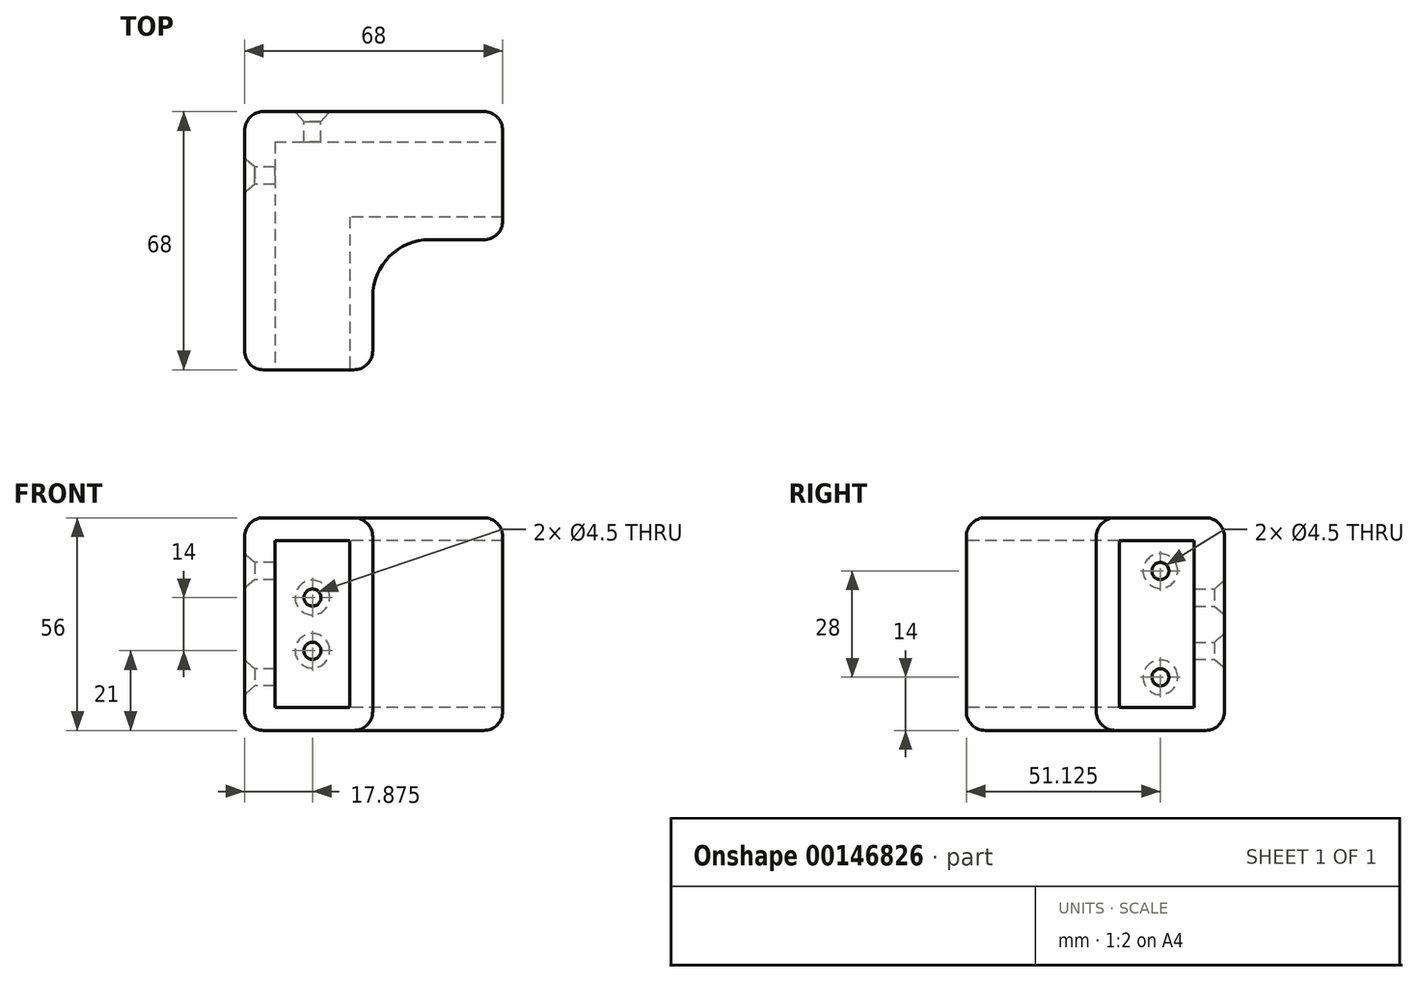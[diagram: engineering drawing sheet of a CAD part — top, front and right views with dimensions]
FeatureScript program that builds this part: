
annotation { "Feature Type Name" : "Feature", "Feature Type Description" : "" }
export const myFeature = defineFeature(function(context is Context, id is Id, definition is map)
    precondition{}
    {
        {
            var Q0;
            Q0=qCreatedBy(makeId("Top.planeOp"),FACE);
            var sketch = newSketch(context, id + "F0", { "sketchPlane" : qUnion([Q0])});
            skLineSegment(sketch, "E0.top", {"start": v(0, -60) * mm, "end": v(19.75, -60) * mm});
            skLineSegment(sketch, "E0.left", {"start": v(0, 0) * mm, "end": v(0, -60) * mm});
            skLineSegment(sketch, "E0.right", {"start": v(19.75, -19.75) * mm, "end": v(19.75, -60) * mm});
            skLineSegment(sketch, "E1", {"start": v(0, 0) * mm, "end": v(60, 0) * mm});
            skLineSegment(sketch, "E2", {"start": v(60, 0) * mm, "end": v(60, -19.75) * mm});
            skLineSegment(sketch, "E3", {"start": v(60, -19.75) * mm, "end": v(19.75, -19.75) * mm});
            skLineSegment(sketch, "E4.0", {"start": v(-8, 8) * mm, "end": v(60, 8) * mm});
            skLineSegment(sketch, "E4.1", {"start": v(-8, 8) * mm, "end": v(-8, -60) * mm});
            skLineSegment(sketch, "E5.0", {"start": v(25.75, -25.75) * mm, "end": v(25.75, -60) * mm});
            skLineSegment(sketch, "E5.1", {"start": v(60, -25.75) * mm, "end": v(25.75, -25.75) * mm});
            skLineSegment(sketch, "E6", {"start": v(-8, -60) * mm, "end": v(0, -60) * mm});
            skLineSegment(sketch, "E7", {"start": v(19.75, -60) * mm, "end": v(25.75, -60) * mm});
            skLineSegment(sketch, "E8", {"start": v(60, -25.75) * mm, "end": v(60, -19.75) * mm});
            skLineSegment(sketch, "E9", {"start": v(60, 0) * mm, "end": v(60, 8) * mm});
            skSolve(sketch);
        }
        {
            var Q0;
            Q0=makeQuery(id+"F0.imprint","IMPRINT",FACE,{"disambiguationData":[TD([[makeQuery(id+"F0.imprint","IMPRINT",EDGE,{"derivedFrom":sQuery(id+"F0.wireOp",EDGE,"E0.left")}),-1.0]])]});
            var Q1;
            Q1=makeQuery(id+"F0.imprint","IMPRINT",FACE,{"disambiguationData":[TD([[makeQuery(id+"F0.imprint","IMPRINT",EDGE,{"derivedFrom":sQuery(id+"F0.wireOp",EDGE,"E0.right")}),1.0]])]});
            var Q2;
            Q2=makeQuery(id+"F0.imprint","IMPRINT",FACE,{"disambiguationData":[TD([[makeQuery(id+"F0.imprint","IMPRINT",EDGE,{"derivedFrom":sQuery(id+"F0.wireOp",EDGE,"E0.top")}),1.0]])]});
            extrude(context, id + "F1", {"entities" : qUnion([Q0, Q1, Q2]), "depth" : 50 * mm, "hasSecondDirection" : true, "secondDirectionOppositeDirection" : true, "secondDirectionDepth" : 6 * mm});
        }
        {
            var Q0;
            Q0=makeQuery(id+"F0.imprint","IMPRINT",FACE,{"disambiguationData":[TD([[makeQuery(id+"F0.imprint","IMPRINT",EDGE,{"derivedFrom":sQuery(id+"F0.wireOp",EDGE,"E0.top")}),1.0]])]});
            extrude(context, id + "F2", {"entities" : qUnion([Q0]), "operationType" : NewBodyOperationType.REMOVE, "depth" : 44 * mm});
        }
        {
            var Q0;
            Q0=makeQuery(id+"F1.opExtrude","SWEPT_FACE",FACE,{"disambiguationData":[OSD([sQuery(id+"F0.wireOp",EDGE,"E4.0")])]});
            var sketch = newSketch(context, id + "F3", { "sketchPlane" : qUnion([Q0])});
            skLineSegment(sketch, "E10.0", {"start": v(0, 44) * mm, "end": v(-19.75, 44) * mm});
            skLineSegment(sketch, "E10.1", {"start": v(-19.75, 44) * mm, "end": v(-19.75, 0) * mm});
            skLineSegment(sketch, "E10.2", {"start": v(0, 44) * mm, "end": v(0, 0) * mm});
            skLineSegment(sketch, "E10.3", {"start": v(8, 0) * mm, "end": v(-60, 0) * mm});
            skLineSegment(sketch, "E11", {"start": v(-9.88, 44) * mm, "end": v(-9.87, 0) * mm, "construction": true});
            skPoint(sketch, "E12", {"position": v(-9.88, 29) * mm});
            skPoint(sketch, "E13", {"position": v(-9.88, 15) * mm});
            skSolve(sketch);
        }
        {
            var Q0;
            Q0=makeQuery(id+"F1.opExtrude","SWEPT_FACE",FACE,{"disambiguationData":[OSD([sQuery(id+"F0.wireOp",EDGE,"E4.1")])]});
            var sketch = newSketch(context, id + "F4", { "sketchPlane" : qUnion([Q0])});
            skLineSegment(sketch, "E14.0.0", {"start": v(25.75, -6) * mm, "end": v(-8, -6) * mm});
            skLineSegment(sketch, "E14.0.1", {"start": v(-8, -6) * mm, "end": v(-8, 50) * mm});
            skLineSegment(sketch, "E14.0.2", {"start": v(-8, 50) * mm, "end": v(25.75, 50) * mm});
            skLineSegment(sketch, "E14.0.3", {"start": v(25.75, 50) * mm, "end": v(25.75, -6) * mm});
            skLineSegment(sketch, "E15", {"start": v(8.87, 50) * mm, "end": v(8.88, -6) * mm, "construction": true});
            skLineSegment(sketch, "E16.0", {"start": v(19.75, 44) * mm, "end": v(19.75, 0) * mm});
            skLineSegment(sketch, "E16.1", {"start": v(0, 44) * mm, "end": v(19.75, 44) * mm});
            skLineSegment(sketch, "E16.2", {"start": v(0, 44) * mm, "end": v(0, 0) * mm});
            skLineSegment(sketch, "E16.3", {"start": v(0, 0) * mm, "end": v(19.75, 0) * mm});
            skPoint(sketch, "E17", {"position": v(8.87, 36) * mm});
            skPoint(sketch, "E18", {"position": v(8.87, 8) * mm});
            skSolve(sketch);
        }
        {
            var Q0;
            Q0=sQuery(id+"F4.wireOp",VERTEX,"E17");
            var Q1;
            Q1=sQuery(id+"F4.wireOp",VERTEX,"E18");
            var Q2;
            Q2=sQuery(id+"F3.wireOp",VERTEX,"E12");
            var Q3;
            Q3=sQuery(id+"F3.wireOp",VERTEX,"E13");
            var Q4;
            Q4=makeQuery(id+"F1.opExtrude","SWEPT_BODY",BODY,{"disambiguationData":[OSD([sQuery(id+"F0.wireOp",EDGE,"E0.top"),sQuery(id+"F0.wireOp",EDGE,"E2"),sQuery(id+"F0.wireOp",EDGE,"E4.0"),sQuery(id+"F0.wireOp",EDGE,"E4.1"),sQuery(id+"F0.wireOp",EDGE,"E5.0"),sQuery(id+"F0.wireOp",EDGE,"E5.1"),sQuery(id+"F0.wireOp",EDGE,"E6"),sQuery(id+"F0.wireOp",EDGE,"E7"),sQuery(id+"F0.wireOp",EDGE,"E8"),sQuery(id+"F0.wireOp",EDGE,"E9")])]});
            hole(context, id + "F5", {"style" : HoleStyle.C_SINK, "endStyle" : HoleEndStyle.THROUGH, "standardTappedOrClearance" : lookupTablePath({ "standard" : "ANSI", "fit" : "Normal (ASME)", "size" : "#8", "type" : "Clearance" }), "standardBlindInLast" : lookupTablePath({ "fit" : "Free", "standard" : "ANSI", "size" : "#8", "type" : "Clearance" }), "holeDiameter" : 4.5 * mm, "cSinkDiameter" : 9.12 * mm, "cSinkAngle" : 82 * degree, "locations" : qUnion([Q0, Q1, Q2, Q3]), "scope" : qUnion([Q4]), "isTappedThrough" : true});
        }
        {
            var Q0;
            Q0=makeQuery(id+"F1.opExtrude","SWEPT_EDGE",EDGE,{"disambiguationData":[OSD([sQuery(id+"F0.wireOp",EDGE,"E5.0"),sQuery(id+"F0.wireOp",EDGE,"E5.1")])]});
            fillet(context, id + "F6", {"entities" : qUnion([Q0]), "radius" : 15 * mm, "tangentPropagation" : true, "allowEdgeOverflow" : false});
        }
        {
            var Q0;
            Q0=makeQuery(id+"F1.opExtrude","CAP_FACE",FACE,{"disambiguationData":[OSD([sQuery(id+"F0.wireOp",EDGE,"E0.top"),sQuery(id+"F0.wireOp",EDGE,"E2"),sQuery(id+"F0.wireOp",EDGE,"E4.0"),sQuery(id+"F0.wireOp",EDGE,"E4.1"),sQuery(id+"F0.wireOp",EDGE,"E5.0"),sQuery(id+"F0.wireOp",EDGE,"E5.1"),sQuery(id+"F0.wireOp",EDGE,"E6"),sQuery(id+"F0.wireOp",EDGE,"E7"),sQuery(id+"F0.wireOp",EDGE,"E8"),sQuery(id+"F0.wireOp",EDGE,"E9")])],"isStart":false});
            var Q1;
            Q1=makeQuery(id+"F1.opExtrude","CAP_FACE",FACE,{"disambiguationData":[OSD([sQuery(id+"F0.wireOp",EDGE,"E0.top"),sQuery(id+"F0.wireOp",EDGE,"E2"),sQuery(id+"F0.wireOp",EDGE,"E4.0"),sQuery(id+"F0.wireOp",EDGE,"E4.1"),sQuery(id+"F0.wireOp",EDGE,"E5.0"),sQuery(id+"F0.wireOp",EDGE,"E5.1"),sQuery(id+"F0.wireOp",EDGE,"E6"),sQuery(id+"F0.wireOp",EDGE,"E7"),sQuery(id+"F0.wireOp",EDGE,"E8"),sQuery(id+"F0.wireOp",EDGE,"E9")])],"isStart":true});
            var Q2;
            Q2=makeQuery(id+"F1.opExtrude","SWEPT_EDGE",EDGE,{"disambiguationData":[OSD([sQuery(id+"F0.wireOp",EDGE,"E5.1"),sQuery(id+"F0.wireOp",EDGE,"E8")])]});
            var Q3;
            Q3=makeQuery(id+"F1.opExtrude","SWEPT_EDGE",EDGE,{"disambiguationData":[OSD([sQuery(id+"F0.wireOp",EDGE,"E4.0"),sQuery(id+"F0.wireOp",EDGE,"E9")])]});
            var Q4;
            Q4=makeQuery(id+"F1.opExtrude","SWEPT_EDGE",EDGE,{"disambiguationData":[OSD([sQuery(id+"F0.wireOp",EDGE,"E5.0"),sQuery(id+"F0.wireOp",EDGE,"E7")])]});
            var Q5;
            Q5=makeQuery(id+"F1.opExtrude","SWEPT_EDGE",EDGE,{"disambiguationData":[OSD([sQuery(id+"F0.wireOp",EDGE,"E4.1"),sQuery(id+"F0.wireOp",EDGE,"E6")])]});
            var Q6;
            Q6=makeQuery(id+"F1.opExtrude","SWEPT_EDGE",EDGE,{"disambiguationData":[OSD([sQuery(id+"F0.wireOp",EDGE,"E4.0"),sQuery(id+"F0.wireOp",EDGE,"E4.1")])]});
            fillet(context, id + "F7", {"entities" : qUnion([Q0, Q1, Q2, Q3, Q4, Q5, Q6]), "radius" : 5 * mm, "tangentPropagation" : true, "allowEdgeOverflow" : false});
        }
    });
